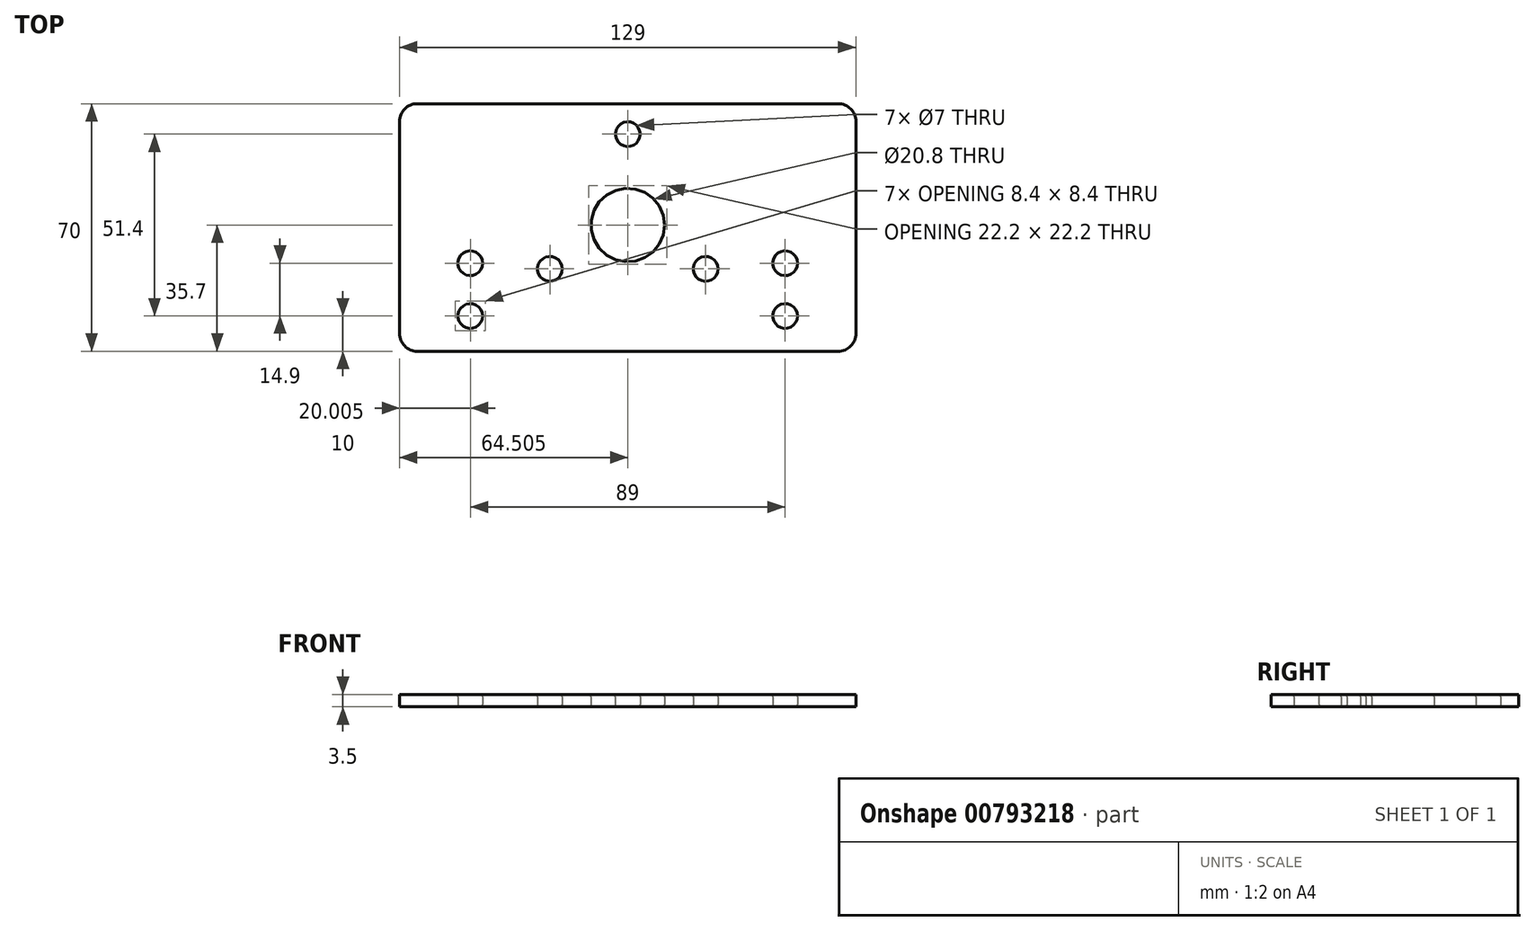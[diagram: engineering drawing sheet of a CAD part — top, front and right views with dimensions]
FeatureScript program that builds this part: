
annotation { "Feature Type Name" : "Feature", "Feature Type Description" : "" }
export const myFeature = defineFeature(function(context is Context, id is Id, definition is map)
    precondition{}
    {
        {
            var Q0;
            Q0=qCreatedBy(makeId("Top.planeOp"),FACE);
            var sketch = newSketch(context, id + "F0", { "sketchPlane" : qUnion([Q0])});
            skLineSegment(sketch, "E0.bottom", {"start": v(-79.33, 31.87) * mm, "end": v(44.67, 31.87) * mm});
            skLineSegment(sketch, "E0.top", {"start": v(-74.33, -38.13) * mm, "end": v(44.67, -38.13) * mm});
            skLineSegment(sketch, "E0.left", {"start": v(-79.33, 26.87) * mm, "end": v(-79.33, -38.13) * mm});
            skLineSegment(sketch, "E0.right", {"start": v(49.67, 26.87) * mm, "end": v(49.67, -33.13) * mm});
            skLineSegment(sketch, "E1", {"start": v(-74.33, 31.87) * mm, "end": v(-14.83, 31.87) * mm, "construction": true});
            skLineSegment(sketch, "E2", {"start": v(-14.83, -38.13) * mm, "end": v(-14.83, -2.43) * mm, "construction": true});
            skCircle(sketch, "E3", {"center": v(-14.83, -2.43) * mm, "radius": 10.4 * mm});
            skLineSegment(sketch, "E4", {"start": v(-14.83, 31.87) * mm, "end": v(-14.83, 23.27) * mm, "construction": true});
            skLineSegment(sketch, "E5", {"start": v(-14.83, 23.27) * mm, "end": v(-36.83, -14.84) * mm, "construction": true});
            skLineSegment(sketch, "E6", {"start": v(-36.83, -14.84) * mm, "end": v(7.17, -14.84) * mm, "construction": true});
            skLineSegment(sketch, "E7", {"start": v(7.17, -14.84) * mm, "end": v(-14.83, 23.27) * mm, "construction": true});
            skCircle(sketch, "E8", {"center": v(-36.83, -14.84) * mm, "radius": 3.5 * mm});
            skCircle(sketch, "E9", {"center": v(7.17, -14.84) * mm, "radius": 3.5 * mm});
            skCircle(sketch, "E10", {"center": v(-14.83, 23.27) * mm, "radius": 3.5 * mm});
            skLineSegment(sketch, "E11", {"start": v(-79.33, -33.13) * mm, "end": v(-79.33, -28.13) * mm, "construction": true});
            skLineSegment(sketch, "E12", {"start": v(-79.33, -28.13) * mm, "end": v(-59.33, -28.13) * mm, "construction": true});
            skLineSegment(sketch, "E13", {"start": v(-59.33, -28.13) * mm, "end": v(-59.33, -13.23) * mm, "construction": true});
            skCircle(sketch, "E14", {"center": v(-59.33, -28.13) * mm, "radius": 3.5 * mm});
            skCircle(sketch, "E15", {"center": v(-59.33, -13.23) * mm, "radius": 3.5 * mm});
            skCircle(sketch, "E16.MirrorC", {"center": v(29.67, -28.13) * mm, "radius": 3.5 * mm});
            skCircle(sketch, "E17.MirrorC", {"center": v(29.67, -13.23) * mm, "radius": 3.5 * mm});
            skLineSegment(sketch, "E18.MirrorCS", {"start": v(29.67, -28.13) * mm, "end": v(29.67, -13.23) * mm, "construction": true});
            skLineSegment(sketch, "E19.MirrorCS", {"start": v(49.67, -28.13) * mm, "end": v(29.67, -28.13) * mm, "construction": true});
            skPoint(sketch, "E20.visualSharp", {"position": v(-79.33, 31.87) * mm});
            skArc(sketch, "E20.filletArc", {"start": v(-74.33, 31.87) * mm, "mid": v(-77.86, 30.4) * mm, "end": v(-79.33, 26.87) * mm});
            skPoint(sketch, "E21.visualSharp", {"position": v(-79.33, -38.13) * mm});
            skArc(sketch, "E21.filletArc", {"start": v(-79.33, -33.13) * mm, "mid": v(-77.86, -36.67) * mm, "end": v(-74.33, -38.13) * mm});
            skPoint(sketch, "E22.visualSharp", {"position": v(49.67, 31.87) * mm});
            skArc(sketch, "E22.filletArc", {"start": v(49.67, 26.87) * mm, "mid": v(48.21, 30.4) * mm, "end": v(44.67, 31.87) * mm});
            skPoint(sketch, "E23.visualSharp", {"position": v(49.67, -38.13) * mm});
            skArc(sketch, "E23.filletArc", {"start": v(44.67, -38.13) * mm, "mid": v(48.21, -36.67) * mm, "end": v(49.67, -33.13) * mm});
            skSolve(sketch);
        }
        {
            var Q0;
            Q0=makeQuery(id+"F0.imprint","IMPRINT",FACE,{"disambiguationData":[TD([[makeQuery(id+"F0.imprint","IMPRINT",EDGE,{"derivedFrom":sQuery(id+"F0.wireOp",EDGE,"E0.top")}),1.0]])]});
            extrude(context, id + "F1", {"entities" : qUnion([Q0]), "depth" : 3.5 * mm, "offsetDistance" : 25 * mm});
        }
        {
            var Q0;
            Q0=makeQuery(id+"F1.opExtrude","CAP_EDGE",EDGE,{"disambiguationData":[OSD([sQuery(id+"F0.wireOp",EDGE,"E15")])],"isStart":false});
            var Q1;
            Q1=makeQuery(id+"F1.opExtrude","CAP_EDGE",EDGE,{"disambiguationData":[OSD([sQuery(id+"F0.wireOp",EDGE,"E14")])],"isStart":false});
            var Q2;
            Q2=makeQuery(id+"F1.opExtrude","CAP_EDGE",EDGE,{"disambiguationData":[OSD([sQuery(id+"F0.wireOp",EDGE,"E8")])],"isStart":false});
            var Q3;
            Q3=makeQuery(id+"F1.opExtrude","CAP_EDGE",EDGE,{"disambiguationData":[OSD([sQuery(id+"F0.wireOp",EDGE,"E10")])],"isStart":false});
            var Q4;
            Q4=makeQuery(id+"F1.opExtrude","CAP_EDGE",EDGE,{"disambiguationData":[OSD([sQuery(id+"F0.wireOp",EDGE,"E3")])],"isStart":false});
            var Q5;
            Q5=makeQuery(id+"F1.opExtrude","CAP_EDGE",EDGE,{"disambiguationData":[OSD([sQuery(id+"F0.wireOp",EDGE,"E9")])],"isStart":false});
            var Q6;
            Q6=makeQuery(id+"F1.opExtrude","CAP_EDGE",EDGE,{"disambiguationData":[OSD([sQuery(id+"F0.wireOp",EDGE,"E16.MirrorC")])],"isStart":false});
            var Q7;
            Q7=makeQuery(id+"F1.opExtrude","CAP_EDGE",EDGE,{"disambiguationData":[OSD([sQuery(id+"F0.wireOp",EDGE,"E17.MirrorC")])],"isStart":false});
            fillet(context, id + "F2", {"entities" : qUnion([Q0, Q1, Q2, Q3, Q4, Q5, Q6, Q7]), "radius" : 0.7 * mm, "tangentPropagation" : true, "rho" : 0.5, "crossSection" : FilletCrossSection.CONIC, "allowEdgeOverflow" : false});
        }
        {
            var Q0;
            Q0=makeQuery(id+"F1.opExtrude","CAP_EDGE",EDGE,{"disambiguationData":[OSD([sQuery(id+"F0.wireOp",EDGE,"E14")])],"isStart":true});
            var Q1;
            Q1=makeQuery(id+"F1.opExtrude","CAP_EDGE",EDGE,{"disambiguationData":[OSD([sQuery(id+"F0.wireOp",EDGE,"E8")])],"isStart":true});
            var Q2;
            Q2=makeQuery(id+"F1.opExtrude","CAP_EDGE",EDGE,{"disambiguationData":[OSD([sQuery(id+"F0.wireOp",EDGE,"E15")])],"isStart":true});
            var Q3;
            Q3=makeQuery(id+"F1.opExtrude","CAP_EDGE",EDGE,{"disambiguationData":[OSD([sQuery(id+"F0.wireOp",EDGE,"E9")])],"isStart":true});
            var Q4;
            Q4=makeQuery(id+"F1.opExtrude","CAP_EDGE",EDGE,{"disambiguationData":[OSD([sQuery(id+"F0.wireOp",EDGE,"E16.MirrorC")])],"isStart":true});
            var Q5;
            Q5=makeQuery(id+"F1.opExtrude","CAP_EDGE",EDGE,{"disambiguationData":[OSD([sQuery(id+"F0.wireOp",EDGE,"E17.MirrorC")])],"isStart":true});
            var Q6;
            Q6=makeQuery(id+"F1.opExtrude","CAP_EDGE",EDGE,{"disambiguationData":[OSD([sQuery(id+"F0.wireOp",EDGE,"E10")])],"isStart":true});
            var Q7;
            Q7=makeQuery(id+"F1.opExtrude","CAP_EDGE",EDGE,{"disambiguationData":[OSD([sQuery(id+"F0.wireOp",EDGE,"E3")])],"isStart":true});
            fillet(context, id + "F3", {"entities" : qUnion([Q0, Q1, Q2, Q3, Q4, Q5, Q6, Q7]), "radius" : 0.7 * mm, "tangentPropagation" : true, "rho" : 0.5, "crossSection" : FilletCrossSection.CONIC, "allowEdgeOverflow" : false});
        }
    });
